# Revit family: 31001F-crown-flush-mount-46-lighting-revit-family
name_source: partatom
category: Lighting Fixtures
units: mm (PartAtom-declared; Revit-internal decimal feet)

## family parameters
Always vertical = Yes
Cut with Voids When Loaded = No
Host = Ceiling
Light Source = Yes
Maintain Annotation Orientation = No
OmniClass Number = 23.80.70.11
OmniClass Title = Luminaries for Internal Lighting
Part Type = Normal
Room Calculation Point = No
Round Connector Dimension = Use Diameter
Shared = No

## types (1)
- 31001F, Crown Flush Mount 46"
    Apparent Load = 120 VA
    Color Filter = 16777215
    Default Elevation = 0 "
    Dimming Lamp Color Temperature Shift = <None>
    Lamp = E26
    Light Source Symbol Size = 7.6 "
    Light source elev (calc) = 7.664 "
    Manufacturer = Dutton Brown
    Model = Crown Flush Mount 46"
    SKU = 31001F
    URL = https://www.duttonbrown.com
    Wattage Comments = 15W

## geometry (parser evidence)
native form markers: Sweep x10
no freeform markers — native parametric forms only
